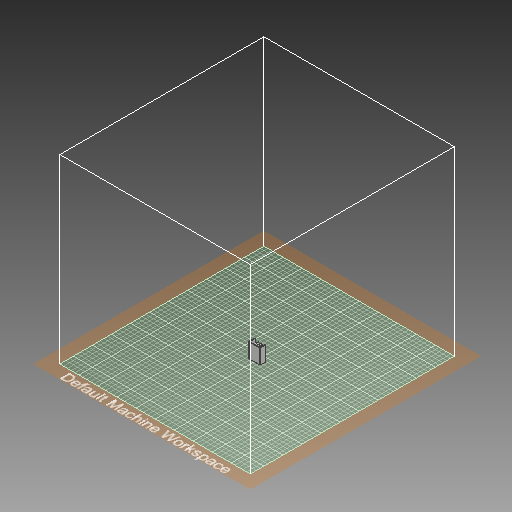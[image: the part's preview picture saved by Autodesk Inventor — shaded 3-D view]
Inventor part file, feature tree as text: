
AUTODESK INVENTOR PART (.ipt)
format: ipt  version: 2019.3 (Build 233278000, 278)  size: 1,131,008 bytes
history: native  units: mm
features: extrude x4, sketch x4, mirror x1, projected_geometry x1
ambient origin geometry x8: Origin, YZ Plane, XZ Plane, XY Plane, X Axis, Y Axis, Z Axis, Center Point
bodies: Body1 (feature_tree)
feature tree (10):
  extrude  "Extrusion2"  Depth=0.5mm
  extrude  "Extrusion4"  Depth=0.5mm
  mirror  "Mirror1"
  extrude  "Extrusion5"  Depth=0.5mm
  extrude  "Extrusion6"  Depth=1.0mm TaperAngle=360.0deg
  sketch  "Sketch5"  dims[d9=30.0deg d10=400.0mm d12=360.0deg d14=10.0mm d15=0.0mm d16=0.15mm d17=15.0mm d20=22.68928mm d21=2.0mm d22=2.0mm d23=10.0mm d24=10.0mm d25=2.0mm d26=4.0mm d27=2.0mm d28=1.0mm d29=1.0mm d30=1.0mm d31=1.0mm d32=11.0mm d34=10.0mm d35=0.0mm d36=3.0mm d37=0.0mm d38=1.0mm d39=0.0mm]
  sketch  "Sketch2"  dims[d3=5.047545mm d4=0.5mm]
  projected_geometry  "Projected Loop1"
  sketch  "Sketch3"  dims[d5=0.5mm d6=0.5mm]
  sketch  "Sketch4"  dims[d7=60.0deg d8=0.5mm]
